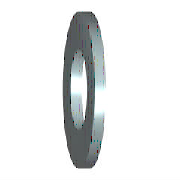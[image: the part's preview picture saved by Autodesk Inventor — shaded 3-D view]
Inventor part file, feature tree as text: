
AUTODESK INVENTOR PART (.ipt)
format: ipt  version: 2016 (Build 200138000, 138)  size: 105,472 bytes
history: native  units: mm (DEFAULTED — no unit token found)
features: other x1, plane x1, sketch x1
ambient origin geometry x7: Origin, YZ Plane, XY Plane, X Axis, Y Axis, Z Axis, Center Point
bodies: Solid1 (feature_tree), Body (feature_tree)
feature tree (3):
  other  "Work Axis1"
  plane  "Work Plane1"
  sketch  "Sketch"  dims[d0=10.5mm d1=20.0mm d2=2.0mm d3=0.0mm d4=0.0mm d5=0.0mm d6=0.0mm d7=0.0mm]
